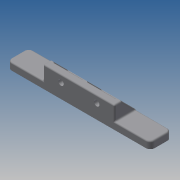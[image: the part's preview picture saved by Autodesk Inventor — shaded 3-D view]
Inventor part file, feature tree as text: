
AUTODESK INVENTOR PART (.ipt)
format: ipt  version: 2014 (Build 180170000, 170)  size: 311,808 bytes
history: native  units: mm
features: extrude x4, sketch x4, fillet x3, mirror x1
ambient origin geometry x8: Origin, YZ Plane, XZ Plane, XY Plane, X Axis, Y Axis, Z Axis, Center Point
bodies: Solid1 (feature_tree)
feature tree (12):
  extrude  "Extrusion1"  Depth=15.0mm
  extrude  "Extrusion2"  Depth=50.0mm
  extrude  "Extrusion3"  Depth=10.0mm
  mirror  "Mirror1"
  extrude  "Extrusion4"  Depth=1.0mm TaperAngle=0.0deg
  fillet  "Fillet1"  Radius=3.0mm
  fillet  "Fillet2"  Radius=3.0mm
  fillet  "Fillet3"  Radius=3.0mm
  sketch  "Sketch1"  dims[d0=100.0mm d1=15.0mm]
  sketch  "Sketch2"  dims[d2=5.0mm d3=0.0mm d4=50.0mm]
  sketch  "Sketch3"  dims[d5=10.0mm d6=3.85mm]
  sketch  "Sketch4"  dims[d7=25.0mm d8=5.0mm d9=0.0mm d10=3.0mm d11=0.0mm d12=3.0mm d13=0.0mm d14=3.0mm d15=1.0mm d16=1.0mm]
